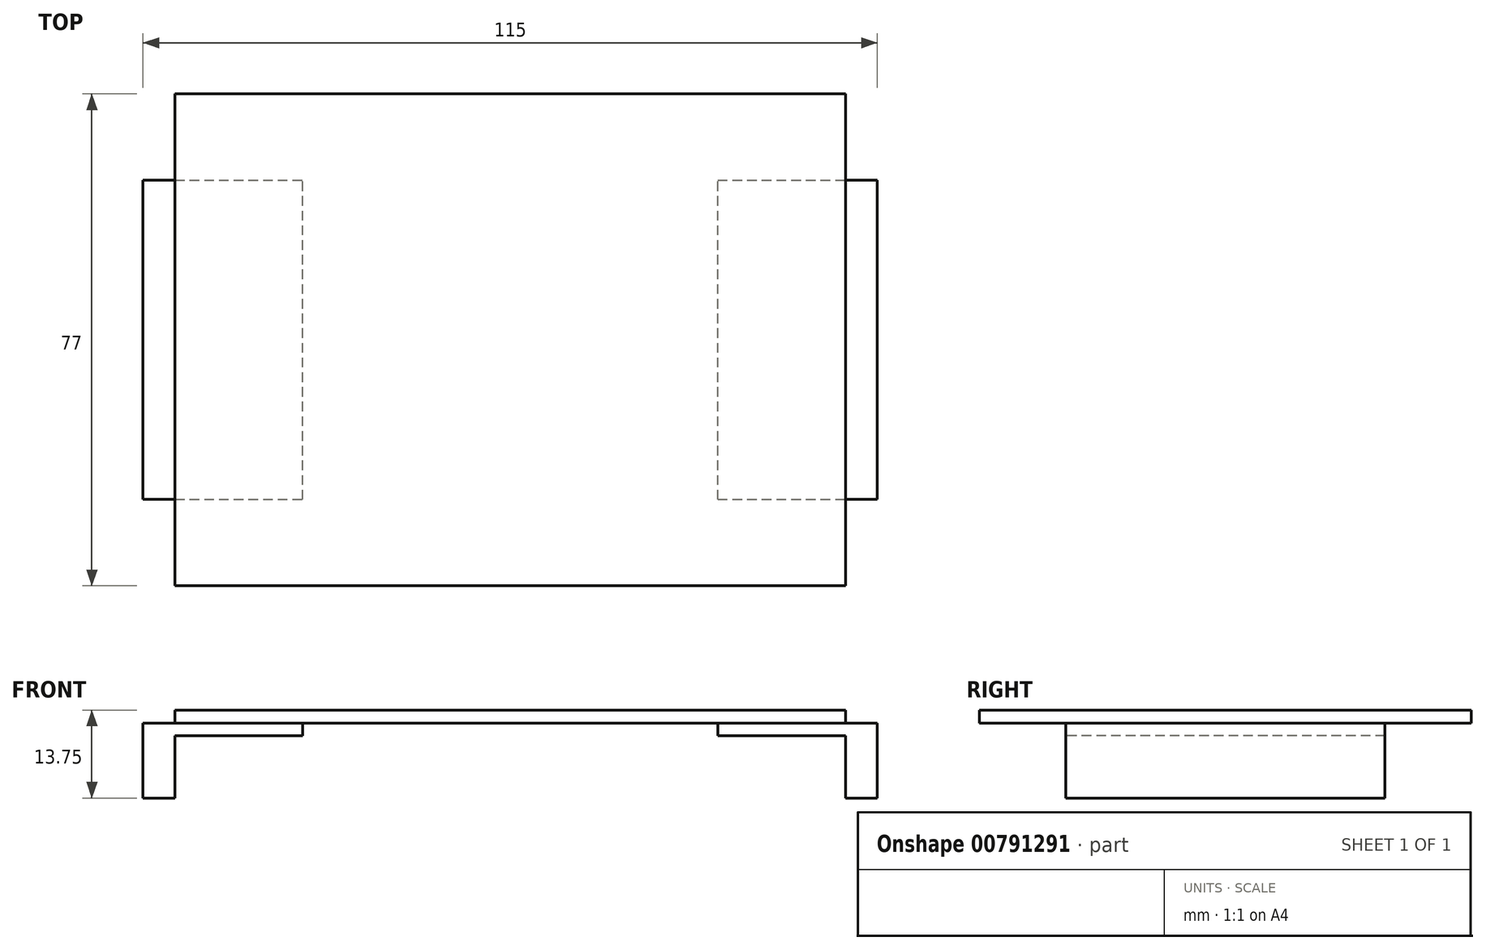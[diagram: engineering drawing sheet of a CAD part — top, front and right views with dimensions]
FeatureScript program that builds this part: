
annotation { "Feature Type Name" : "Feature", "Feature Type Description" : "" }
export const myFeature = defineFeature(function(context is Context, id is Id, definition is map)
    precondition{}
    {
        {
            var Q0;
            Q0=qCreatedBy(makeId("Top.planeOp"),FACE);
            var sketch = newSketch(context, id + "F0", { "sketchPlane" : qUnion([Q0])});
            skLineSegment(sketch, "E0.bottom", {"start": v(-52.5, 38.5) * mm, "end": v(52.5, 38.5) * mm});
            skLineSegment(sketch, "E0.top", {"start": v(-52.5, -38.5) * mm, "end": v(52.5, -38.5) * mm});
            skLineSegment(sketch, "E0.left", {"start": v(-52.5, 38.5) * mm, "end": v(-52.5, -38.5) * mm});
            skLineSegment(sketch, "E0.right", {"start": v(52.5, 38.5) * mm, "end": v(52.5, -38.5) * mm});
            skLineSegment(sketch, "E1.bottom", {"start": v(41.5, 25) * mm, "end": v(46.5, 25) * mm});
            skLineSegment(sketch, "E1.top", {"start": v(41.5, -25) * mm, "end": v(46.5, -25) * mm});
            skLineSegment(sketch, "E1.left", {"start": v(41.5, 25) * mm, "end": v(41.5, -25) * mm});
            skLineSegment(sketch, "E1.right", {"start": v(46.5, 25) * mm, "end": v(46.5, -25) * mm});
            skLineSegment(sketch, "E2.bottom", {"start": v(-57.5, 38.5) * mm, "end": v(57.5, 38.5) * mm});
            skLineSegment(sketch, "E2.top", {"start": v(-57.5, -38.5) * mm, "end": v(57.5, -38.5) * mm});
            skLineSegment(sketch, "E2.left", {"start": v(-57.5, 38.5) * mm, "end": v(-57.5, -38.5) * mm});
            skLineSegment(sketch, "E2.right", {"start": v(57.5, 38.5) * mm, "end": v(57.5, -38.5) * mm});
            skSolve(sketch);
        }
        {
            var Q0;
            {var subQ1=sQuery(id+"F0.wireOp",EDGE,"E0.left");Q0=makeQuery(id+"F0.imprint","IMPRINT",FACE,{"disambiguationData":[TD([[makeQuery(id+"F0.imprint","IMPRINT",EDGE,{"derivedFrom":subQ1}),1.0]])]});}
            var sketch = newSketch(context, id + "F1", { "sketchPlane" : qUnion([Q0])});
            skLineSegment(sketch, "E3.bottom", {"start": v(-57.5, -25) * mm, "end": v(-32.5, -25) * mm});
            skLineSegment(sketch, "E3.top", {"start": v(-57.5, 25) * mm, "end": v(-32.5, 25) * mm});
            skLineSegment(sketch, "E3.left", {"start": v(-57.5, -25) * mm, "end": v(-57.5, 25) * mm});
            skLineSegment(sketch, "E3.right", {"start": v(-32.5, -25) * mm, "end": v(-32.5, 25) * mm});
            skLineSegment(sketch, "E4.bottom", {"start": v(32.5, -25) * mm, "end": v(57.5, -25) * mm});
            skLineSegment(sketch, "E4.top", {"start": v(32.5, 25) * mm, "end": v(57.5, 25) * mm});
            skLineSegment(sketch, "E4.left", {"start": v(32.5, -25) * mm, "end": v(32.5, 25) * mm});
            skLineSegment(sketch, "E4.right", {"start": v(57.5, -25) * mm, "end": v(57.5, 25) * mm});
            skSolve(sketch);
        }
        {
            var Q0;
            {var subQ1=sQuery(id+"F0.wireOp",EDGE,"E0.left");Q0=makeQuery(id+"F0.imprint","IMPRINT",FACE,{"disambiguationData":[TD([[makeQuery(id+"F0.imprint","IMPRINT",EDGE,{"derivedFrom":subQ1}),1.0]])]});}
            var Q1;
            Q1=makeQuery(id+"F0.imprint","IMPRINT",FACE,{"disambiguationData":[TD([[makeQuery(id+"F0.imprint","IMPRINT",EDGE,{"derivedFrom":sQuery(id+"F0.wireOp",EDGE,"E1.bottom")}),-1.0]])]});
            extrude(context, id + "F2", {"entities" : qUnion([Q0, Q1]), "depth" : 2 * mm, "offsetDistance" : 25 * mm});
        }
        {
            var Q0;
            {var subQ0=sQuery(id+"F1.wireOp",EDGE,"E3.left");Q0=makeQuery(id+"F1.imprint","IMPRINT",FACE,{"disambiguationData":[TD([[makeQuery(id+"F1.imprint","IMPRINT",EDGE,{"derivedFrom":subQ0}),-1.0]])]});}
            var Q1;
            {var subQ0=sQuery(id+"F1.wireOp",EDGE,"E4.right");Q1=makeQuery(id+"F1.imprint","IMPRINT",FACE,{"disambiguationData":[TD([[makeQuery(id+"F1.imprint","IMPRINT",EDGE,{"derivedFrom":subQ0}),1.0]])]});}
            extrude(context, id + "F3", {"entities" : qUnion([Q0, Q1]), "operationType" : NewBodyOperationType.ADD, "oppositeDirection" : true, "depth" : 11.75 * mm, "offsetDistance" : 25 * mm});
        }
        {
            var Q0;
            {var subQ0=sQuery(id+"F1.wireOp",EDGE,"E3.right");Q0=makeQuery(id+"F1.imprint","IMPRINT",FACE,{"disambiguationData":[TD([[makeQuery(id+"F1.imprint","IMPRINT",EDGE,{"derivedFrom":subQ0}),1.0]])]});}
            var Q1;
            {var subQ2=sQuery(id+"F1.wireOp",EDGE,"E4.left");Q1=makeQuery(id+"F1.imprint","IMPRINT",FACE,{"disambiguationData":[TD([[makeQuery(id+"F1.imprint","IMPRINT",EDGE,{"derivedFrom":subQ2}),-1.0]])]});}
            var Q2;
            Q2=makeQuery(id+"F0.imprint","IMPRINT",FACE,{"disambiguationData":[TD([[makeQuery(id+"F0.imprint","IMPRINT",EDGE,{"derivedFrom":sQuery(id+"F0.wireOp",EDGE,"E1.bottom")}),-1.0]])]});
            var Q3;
            {var subQ1=makeQuery(id+"F0.imprint","IMPRINT",EDGE,{"derivedFrom":sQuery(id+"F0.wireOp",EDGE,"E1.right")});Q3=makeQuery(id+"F1.imprint","IMPRINT",FACE,{"disambiguationData":[TD([[makeQuery(id+"F1.imprint","IMPRINT",EDGE,{"derivedFrom":subQ1}),1.0]])]});}
            extrude(context, id + "F4", {"entities" : qUnion([Q0, Q1, Q2, Q3]), "operationType" : NewBodyOperationType.ADD, "oppositeDirection" : true, "depth" : 2 * mm, "offsetDistance" : 25 * mm});
        }
    });
